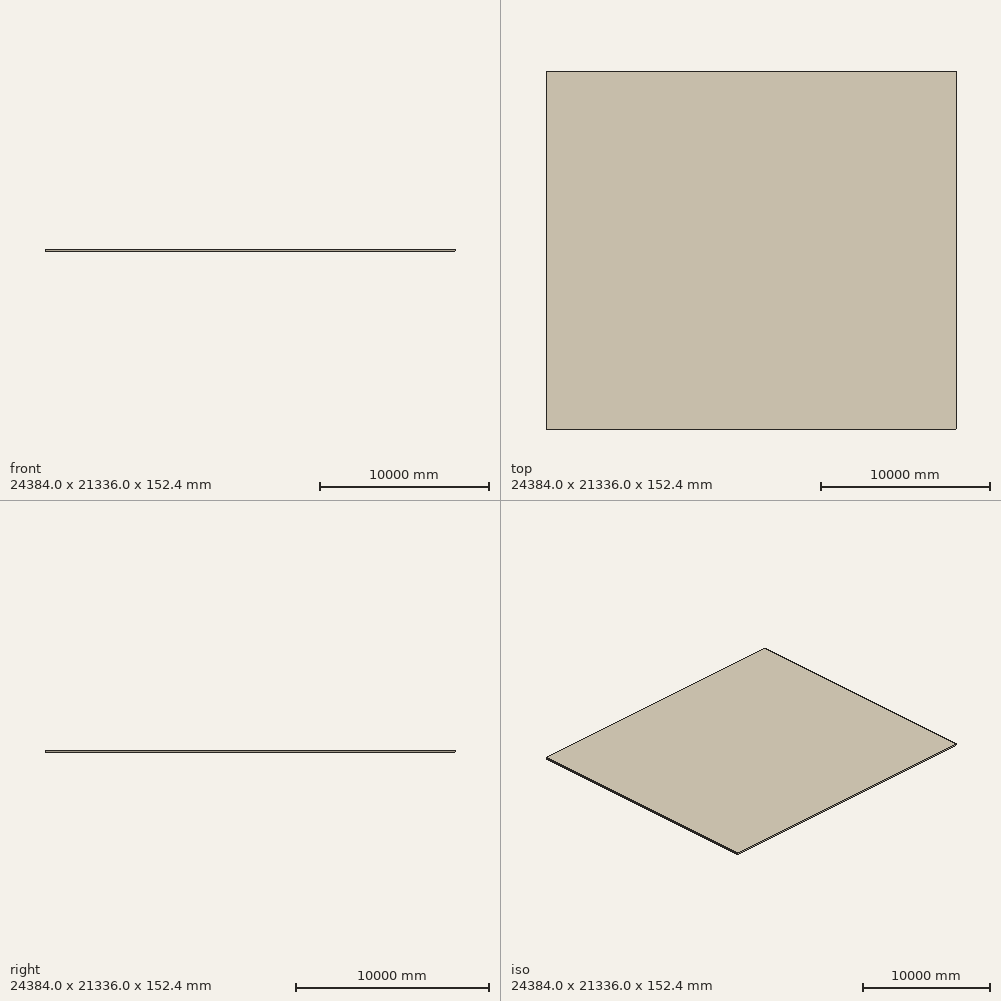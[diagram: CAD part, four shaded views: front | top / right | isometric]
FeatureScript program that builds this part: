
annotation { "Feature Type Name" : "Feature", "Feature Type Description" : "" }
export const myFeature = defineFeature(function(context is Context, id is Id, definition is map)
    precondition{}
    {
        {
            var Q0;
            Q0=qCreatedBy(makeId("Top.planeOp"),FACE);
            var sketch = newSketch(context, id + "F0", { "sketchPlane" : qUnion([Q0])});
            skLineSegment(sketch, "E0.bottom", {"start": v(-12192, 10668) * mm, "end": v(12192, 10668) * mm});
            skLineSegment(sketch, "E0.top", {"start": v(-12192, -10668) * mm, "end": v(12192, -10668) * mm});
            skLineSegment(sketch, "E0.left", {"start": v(-12192, 10668) * mm, "end": v(-12192, -10668) * mm});
            skLineSegment(sketch, "E0.right", {"start": v(12192, 10668) * mm, "end": v(12192, -10668) * mm});
            skPoint(sketch, "E0.middle", {"position": v(0, 0) * mm});
            skSolve(sketch);
        }
        {
            var Q0;
            Q0=makeQuery(id+"F0.imprint","IMPRINT",FACE,{"disambiguationData":[TD([[makeQuery(id+"F0.imprint","IMPRINT",EDGE,{"derivedFrom":sQuery(id+"F0.wireOp",EDGE,"E0.bottom")}),-1.0]])]});
            extrude(context, id + "F1", {"entities" : qUnion([Q0]), "depth" : 152.4 * mm, "offsetDistance" : 25.4 * mm});
        }
    });
